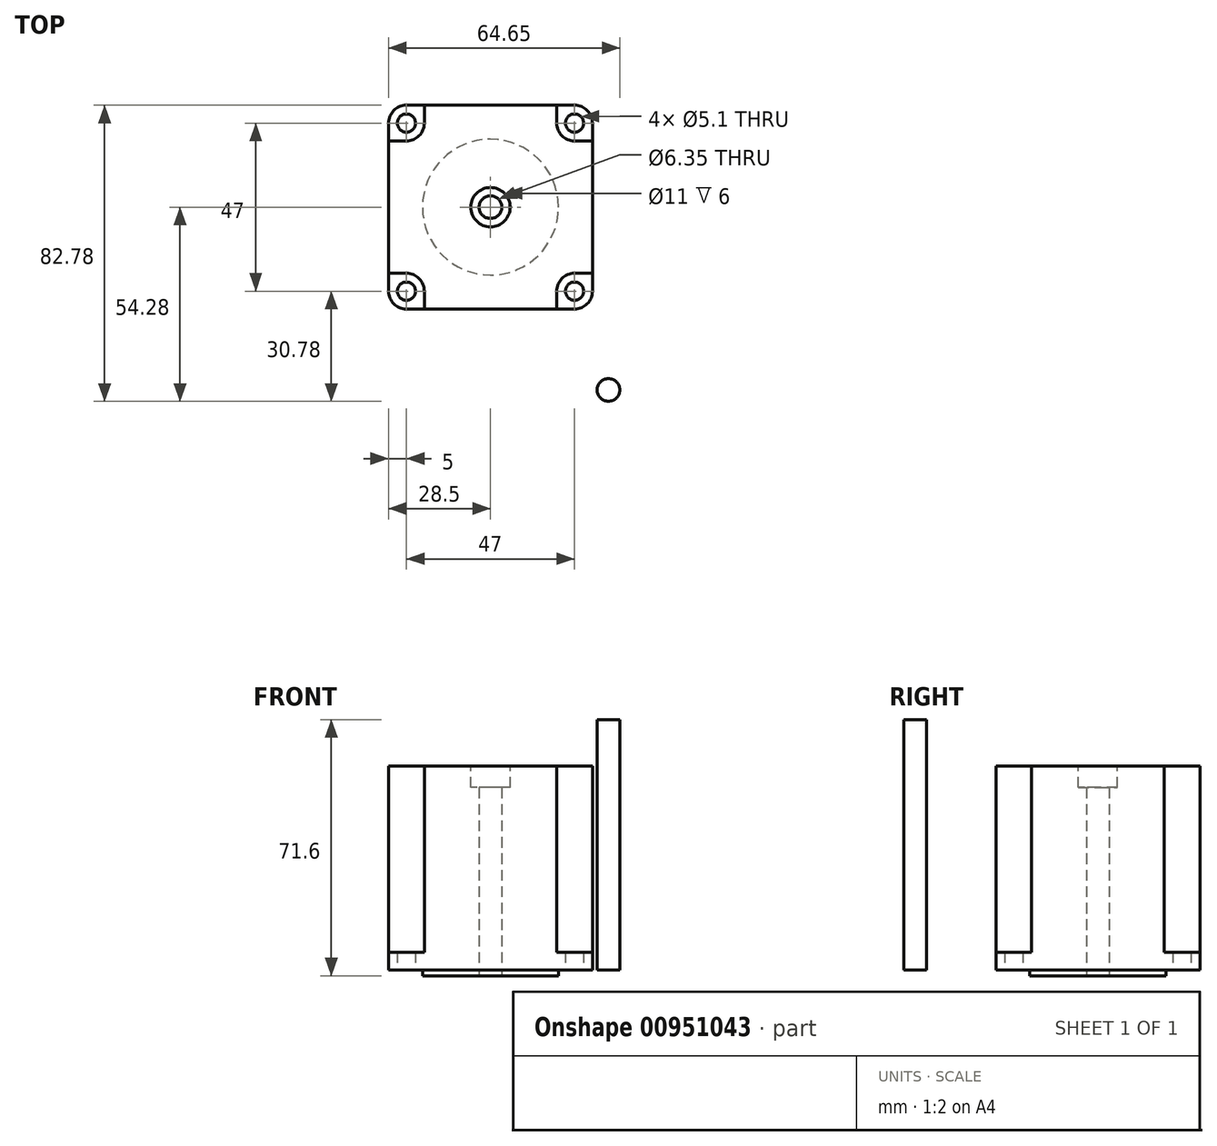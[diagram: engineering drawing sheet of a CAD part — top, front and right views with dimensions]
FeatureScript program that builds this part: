
annotation { "Feature Type Name" : "Feature", "Feature Type Description" : "" }
export const myFeature = defineFeature(function(context is Context, id is Id, definition is map)
    precondition{}
    {
        {
            var Q0;
            Q0=qCreatedBy(makeId("Top.planeOp"),FACE);
            var sketch = newSketch(context, id + "F0", { "sketchPlane" : qUnion([Q0])});
            skLineSegment(sketch, "E0.bottom", {"start": v(23.5, 28.5) * mm, "end": v(-23.5, 28.5) * mm});
            skLineSegment(sketch, "E0.top", {"start": v(23.5, -28.5) * mm, "end": v(-23.5, -28.5) * mm});
            skLineSegment(sketch, "E0.left", {"start": v(28.5, 23.5) * mm, "end": v(28.5, -23.5) * mm});
            skLineSegment(sketch, "E0.right", {"start": v(-28.5, 23.5) * mm, "end": v(-28.5, -23.5) * mm});
            skPoint(sketch, "E0.middle", {"position": v(0, 0) * mm});
            skLineSegment(sketch, "E1.bottom", {"start": v(-23.5, 23.5) * mm, "end": v(23.5, 23.5) * mm, "construction": true});
            skLineSegment(sketch, "E1.top", {"start": v(-23.5, -23.5) * mm, "end": v(23.5, -23.5) * mm, "construction": true});
            skLineSegment(sketch, "E1.left", {"start": v(-23.5, 23.5) * mm, "end": v(-23.5, -23.5) * mm, "construction": true});
            skLineSegment(sketch, "E1.right", {"start": v(23.5, 23.5) * mm, "end": v(23.5, -23.5) * mm, "construction": true});
            skCircle(sketch, "E2", {"center": v(-23.5, 23.5) * mm, "radius": 2.55 * mm});
            skCircle(sketch, "E3", {"center": v(23.5, 23.5) * mm, "radius": 2.55 * mm});
            skCircle(sketch, "E4", {"center": v(23.5, -23.5) * mm, "radius": 2.55 * mm});
            skCircle(sketch, "E5", {"center": v(-23.5, -23.5) * mm, "radius": 2.55 * mm});
            skPoint(sketch, "E6.visualSharp", {"position": v(-28.5, 28.5) * mm});
            skArc(sketch, "E6.filletArc", {"start": v(-23.5, 28.5) * mm, "mid": v(-27.04, 27.04) * mm, "end": v(-28.5, 23.5) * mm});
            skPoint(sketch, "E7.visualSharp", {"position": v(28.5, 28.5) * mm});
            skArc(sketch, "E7.filletArc", {"start": v(28.5, 23.5) * mm, "mid": v(27.04, 27.04) * mm, "end": v(23.5, 28.5) * mm});
            skPoint(sketch, "E8.visualSharp", {"position": v(-28.5, -28.5) * mm});
            skArc(sketch, "E8.filletArc", {"start": v(-28.5, -23.5) * mm, "mid": v(-27.04, -27.04) * mm, "end": v(-23.5, -28.5) * mm});
            skPoint(sketch, "E9.visualSharp", {"position": v(28.5, -28.5) * mm});
            skArc(sketch, "E9.filletArc", {"start": v(23.5, -28.5) * mm, "mid": v(27.04, -27.04) * mm, "end": v(28.5, -23.5) * mm});
            skSolve(sketch);
        }
        {
            var Q0;
            Q0 = qSketchRegion(id + "F0", true);
            extrude(context, id + "F1", {"entities" : qUnion([Q0]), "depth" : 4 * mm, "offsetDistance" : 25 * mm});
        }
        {
            var Q0;
            Q0=makeQuery(id+"F1.opExtrude","CAP_FACE",FACE,{"disambiguationData":[OSD([sQuery(id+"F0.wireOp",EDGE,"E0.bottom"),sQuery(id+"F0.wireOp",EDGE,"E0.top"),sQuery(id+"F0.wireOp",EDGE,"E0.left"),sQuery(id+"F0.wireOp",EDGE,"E0.right"),sQuery(id+"F0.wireOp",EDGE,"E2"),sQuery(id+"F0.wireOp",EDGE,"E3"),sQuery(id+"F0.wireOp",EDGE,"E4"),sQuery(id+"F0.wireOp",EDGE,"E5"),sQuery(id+"F0.wireOp",EDGE,"E6.filletArc"),sQuery(id+"F0.wireOp",EDGE,"E7.filletArc"),sQuery(id+"F0.wireOp",EDGE,"E8.filletArc"),sQuery(id+"F0.wireOp",EDGE,"E9.filletArc")])],"isStart":true});
            var sketch = newSketch(context, id + "F2", { "sketchPlane" : qUnion([Q0])});
            skCircle(sketch, "E10", {"center": v(0, 0) * mm, "radius": 19 * mm});
            skSolve(sketch);
        }
        {
            var Q0;
            Q0 = qSketchRegion(id + "F2", true);
            extrude(context, id + "F3", {"entities" : qUnion([Q0]), "operationType" : NewBodyOperationType.ADD, "depth" : 1.6 * mm, "offsetDistance" : 25 * mm});
        }
        {
            var Q0;
            Q0=makeQuery(id+"F3.opExtrude","CAP_FACE",FACE,{"disambiguationData":[OSD([sQuery(id+"F2.wireOp",EDGE,"E10")])],"isStart":false});
            var sketch = newSketch(context, id + "F4", { "sketchPlane" : qUnion([Q0])});
            skCircle(sketch, "E11", {"center": v(0, 0) * mm, "radius": 3.17 * mm});
            skSolve(sketch);
        }
        {
            var Q0;
            Q0 = qSketchRegion(id + "F4", true);
            extrude(context, id + "F5", {"entities" : qUnion([Q0]), "operationType" : NewBodyOperationType.REMOVE, "oppositeDirection" : true, "depth" : 25 * mm, "offsetDistance" : 25 * mm});
        }
        {
            var Q0;
            Q0=makeQuery(id+"F1.opExtrude","CAP_FACE",FACE,{"disambiguationData":[OSD([sQuery(id+"F0.wireOp",EDGE,"E0.bottom"),sQuery(id+"F0.wireOp",EDGE,"E0.top"),sQuery(id+"F0.wireOp",EDGE,"E0.left"),sQuery(id+"F0.wireOp",EDGE,"E0.right"),sQuery(id+"F0.wireOp",EDGE,"E2"),sQuery(id+"F0.wireOp",EDGE,"E3"),sQuery(id+"F0.wireOp",EDGE,"E4"),sQuery(id+"F0.wireOp",EDGE,"E5"),sQuery(id+"F0.wireOp",EDGE,"E6.filletArc"),sQuery(id+"F0.wireOp",EDGE,"E7.filletArc"),sQuery(id+"F0.wireOp",EDGE,"E8.filletArc"),sQuery(id+"F0.wireOp",EDGE,"E9.filletArc")])],"isStart":false});
            extrude(context, id + "F6", {"entities" : qUnion([Q0]), "operationType" : NewBodyOperationType.ADD, "depth" : 1 * mm, "offsetDistance" : 25 * mm});
        }
        {
            var Q0;
            Q0=makeQuery(id+"F6.opExtrude","CAP_FACE",FACE,{"disambiguationData":[OSD([sQuery(id+"F0.wireOp",EDGE,"E0.bottom"),sQuery(id+"F0.wireOp",EDGE,"E0.top"),sQuery(id+"F0.wireOp",EDGE,"E0.left"),sQuery(id+"F0.wireOp",EDGE,"E0.right"),sQuery(id+"F0.wireOp",EDGE,"E2"),sQuery(id+"F0.wireOp",EDGE,"E3"),sQuery(id+"F0.wireOp",EDGE,"E4"),sQuery(id+"F0.wireOp",EDGE,"E5"),sQuery(id+"F0.wireOp",EDGE,"E6.filletArc"),sQuery(id+"F0.wireOp",EDGE,"E7.filletArc"),sQuery(id+"F0.wireOp",EDGE,"E8.filletArc"),sQuery(id+"F0.wireOp",EDGE,"E9.filletArc")])],"isStart":false});
            var sketch = newSketch(context, id + "F7", { "sketchPlane" : qUnion([Q0])});
            skArc(sketch, "E12", {"start": v(18.5, 23.5) * mm, "mid": v(19.96, 19.96) * mm, "end": v(23.5, 18.5) * mm});
            skLineSegment(sketch, "E13", {"start": v(28.5, 18.5) * mm, "end": v(23.5, 18.5) * mm});
            skLineSegment(sketch, "E14", {"start": v(18.5, 23.5) * mm, "end": v(18.5, 28.5) * mm});
            skLineSegment(sketch, "E15", {"start": v(0, 0) * mm, "end": v(0, 6.12) * mm, "construction": true});
            skLineSegment(sketch, "E16", {"start": v(0, 6.12) * mm, "end": v(0, 0) * mm, "construction": true});
            skLineSegment(sketch, "E17", {"start": v(0, 0) * mm, "end": v(6.06, 0) * mm, "construction": true});
            skLineSegment(sketch, "E18.MirrorCS", {"start": v(18.5, -23.5) * mm, "end": v(18.5, -28.5) * mm});
            skArc(sketch, "E19.MirrorCS", {"start": v(18.5, -23.5) * mm, "mid": v(19.96, -19.96) * mm, "end": v(23.5, -18.5) * mm});
            skLineSegment(sketch, "E20.MirrorCS", {"start": v(28.5, -18.5) * mm, "end": v(23.5, -18.5) * mm});
            skLineSegment(sketch, "E21.MirrorCS", {"start": v(-28.5, 18.5) * mm, "end": v(-23.5, 18.5) * mm});
            skLineSegment(sketch, "E22.MirrorCS", {"start": v(-18.5, 23.5) * mm, "end": v(-18.5, 28.5) * mm});
            skLineSegment(sketch, "E23.MirrorCS", {"start": v(-18.5, -23.5) * mm, "end": v(-18.5, -28.5) * mm});
            skLineSegment(sketch, "E24.MirrorCS", {"start": v(-28.5, -18.5) * mm, "end": v(-23.5, -18.5) * mm});
            skArc(sketch, "E25.MirrorCS", {"start": v(-18.5, -23.5) * mm, "mid": v(-19.96, -19.96) * mm, "end": v(-23.5, -18.5) * mm});
            skArc(sketch, "E26.MirrorCS", {"start": v(-18.5, 23.5) * mm, "mid": v(-19.96, 19.96) * mm, "end": v(-23.5, 18.5) * mm});
            skSolve(sketch);
        }
        {
            var Q0;
            Q0=makeQuery(id+"F7.imprint","IMPRINT",FACE,{"disambiguationData":[TD([[makeQuery(id+"F7.imprint","IMPRINT",EDGE,{"derivedFrom":sQuery(id+"F7.wireOp",EDGE,"E12")}),-1.0]])]});
            extrude(context, id + "F8", {"entities" : qUnion([Q0]), "operationType" : NewBodyOperationType.ADD, "depth" : 52 * mm, "offsetDistance" : 25 * mm});
        }
        {
            var Q0;
            Q0=qCreatedBy(makeId("Top.planeOp"),FACE);
            var sketch = newSketch(context, id + "F9", { "sketchPlane" : qUnion([Q0])});
            skCircle(sketch, "E27", {"center": v(32.98, -51.1) * mm, "radius": 3.17 * mm});
            skSolve(sketch);
        }
        {
            var Q0;
            Q0 = qSketchRegion(id + "F9", true);
            extrude(context, id + "F10", {"entities" : qUnion([Q0]), "depth" : 70 * mm, "offsetDistance" : 25 * mm});
        }
        {
            var Q0;
            Q0=makeQuery(id+"F8.opExtrude","CAP_FACE",FACE,{"disambiguationData":[OSD([sQuery(id+"F0.wireOp",EDGE,"E0.bottom"),sQuery(id+"F0.wireOp",EDGE,"E0.top"),sQuery(id+"F0.wireOp",EDGE,"E0.left"),sQuery(id+"F0.wireOp",EDGE,"E0.right"),sQuery(id+"F0.wireOp",EDGE,"E2"),sQuery(id+"F0.wireOp",EDGE,"E3"),sQuery(id+"F0.wireOp",EDGE,"E4"),sQuery(id+"F0.wireOp",EDGE,"E5"),sQuery(id+"F0.wireOp",EDGE,"E6.filletArc"),sQuery(id+"F0.wireOp",EDGE,"E7.filletArc"),sQuery(id+"F0.wireOp",EDGE,"E8.filletArc"),sQuery(id+"F0.wireOp",EDGE,"E9.filletArc"),sQuery(id+"F4.wireOp",EDGE,"E11"),sQuery(id+"F7.wireOp",EDGE,"E12"),sQuery(id+"F7.wireOp",EDGE,"E13"),sQuery(id+"F7.wireOp",EDGE,"E14"),sQuery(id+"F7.wireOp",EDGE,"E18.MirrorCS"),sQuery(id+"F7.wireOp",EDGE,"E19.MirrorCS"),sQuery(id+"F7.wireOp",EDGE,"E20.MirrorCS"),sQuery(id+"F7.wireOp",EDGE,"E21.MirrorCS"),sQuery(id+"F7.wireOp",EDGE,"E22.MirrorCS"),sQuery(id+"F7.wireOp",EDGE,"E23.MirrorCS"),sQuery(id+"F7.wireOp",EDGE,"E24.MirrorCS"),sQuery(id+"F7.wireOp",EDGE,"E25.MirrorCS"),sQuery(id+"F7.wireOp",EDGE,"E26.MirrorCS")])],"isStart":false});
            var sketch = newSketch(context, id + "F11", { "sketchPlane" : qUnion([Q0])});
            skCircle(sketch, "E28", {"center": v(0, 0) * mm, "radius": 5.5 * mm});
            skSolve(sketch);
        }
        {
            var Q0;
            Q0 = qSketchRegion(id + "F11", true);
            extrude(context, id + "F12", {"entities" : qUnion([Q0]), "operationType" : NewBodyOperationType.REMOVE, "oppositeDirection" : true, "depth" : 6 * mm, "offsetDistance" : 25 * mm});
        }
    });
